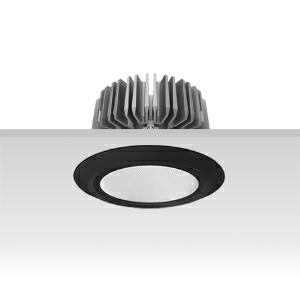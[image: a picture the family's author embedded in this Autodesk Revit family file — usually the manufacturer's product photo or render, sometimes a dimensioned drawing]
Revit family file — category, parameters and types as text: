
# Revit family: 3f_filippi_-_3f_reno_bianco_ampio_3f_filippi_-_30345_a01047_-_3f_reno_150_wh_2000-930_wide___smp_bk_7763
name_source: partatom
category: Lighting Fixtures
units: mm (PartAtom-declared; Revit-internal decimal feet)

## family parameters
Cut with Voids When Loaded = No
Host = Face
Light Source = No
Part Type = Normal
Room Calculation Point = No
Round Connector Dimension = Use Diameter
Shared = No

## types (1)
- 3F Filippi - 3F Reno Bianco Ampio (1 x LED, 1652 lm, 24 W, 3000 K)
    Apparent Load = 24 VA
    Approval mark = CE
    CIE Flux Codes = 73 92 98 100 100
    Color Rendering = 90
    Color Temperature = 3000 K
    Control Gear = Electronic ballast
    Default Elevation = 1800 mm
    Description = ILLUMINOTECHNICAL
Luminous efficiency 100% (DLOR 100%, ULOR 0%).
Initial luminous flux of the luminaire 1652 lm.
Direct symmetric wide distribution.
Installation Interdistance Transv.D = 1.01 x hu - Long.D = 1.00 x hu.
Tabular UGR (CIE 117 - 4H-8H; S=0.25H; 70/50/20): RUG 23.3 - 23.3.
Beam angle: 70° - 70°.
Luminous efficacy 69 lm/W.
Lifetime (L90/B10): 30000 h. (tq+25°C)
Lifetime (L85/B10): 50000 h. (tq+25°C)
Lifetime (L70/B10): 80000 h. (tq+25°C)
Sudden decreased luminous flux after 50000 hours: 0% (C0).
Photobiological safety in compliance with IEC/TR 62778: RG0 risk exempt, (IEC 62471).
In compliance with IEC/EN 62722-2-1 - IEC/EN 62717 standards.

SOURCE
Compact LED module 2000/930.
Energy efficiency class (UE 2019/2020 - UE 2019/2015): E.
CIE 13.3 Colour rendering index: CRI >90 (R9 >50%).
IES TM-30 Fidelity Index: Rf = 92 Rg = 101.
CCT nominal colour temperature 3000 K.
Colour initial tolerance (MacAdam): SDCM 3.
Zhaga Book 3 compliant.

MECHANICAL
Passive heat dissipator in die-casting aluminium, oversized, for optimum thermal management of the LED module.
Parabolic element with graduated/concentric rings in white polycarbonate.
Transparent external lens with glossy and satin differentiated surfaces, with a cooling and anti-insect system in methacrylate (PMMA).
Fastening spring clips in stainless steel.
Dimensions: diameter 176 mm, height 111 mm. Weight 0.75 kg.
IP44 protection degree for exposed part, IP20 for recessed part.
Mechanical strength to impacts IK05 (0.7 joule).
Glow-wire test resistance 650°C.

ELECTRICAL
Wiring on a separate unit.
Halogen Free electronic wiring 230V-50/60Hz, power factor 0.95, THD <25%, constant output current, SELV, class II, 1 driver.
Power of the luminaire 24 W.
ENEC - CE.
SAFE FLICKER: PstLM=<1 and SVM=<0.4 (IEC TR 61547-1 and IEC TR 63158), to ensure a more comfortable and safe light.
Luminaire compliant with EN 60598-2-22 for power supply from a centralised emergency system CPSS (Central Power Supply System), not incorporated in the luminaire - high risk areas excluded. The default power and flux are 100% in AC and 100% in DC.
Ambient temperature from 0°C to +25°C.
Temperature class T6 max 85°C.
Relative humidity UR: <85%.

INSTALLATION
Pull-up recessed fitting.
False ceiling carving: 150 mm.
All accessories dedicated to this product are available on the Catalog and on our website www.3F-Filippi.com.

ACCESSORIES
A01047 - Anti-glare microprismatic SMP diffuser in methacrylate (PMMA), locked and in line with the trim, in black polycarbonate.

APPLICATIONS
Suitable product for food production plants (HACCP), IFS (Food Version 6), BRC (GSFS Food Version 7).
Environments: architectural, commercial, exhibition areas, transit areas, corridors, shops, display windows, service areas.
In false ceilings with narrow voids.

WARNING
Luminaire designed for disposal/recycling at end-of-life.
Replaceable (LED only) light source by a professional. Replaceable control gear by a professional.
    Height = 0 mm  [stored 0 ft]
    Lamp = 1 x LED
    Lamp Light Flux = 1652 lm
    Lamp Power = 24 W
    Lamp count = 1
    Length = 176 mm
    Lifetime = 50000 h
    Luminous efficacy = 69 lm/W
    Manufacturer = 3F Filippi
    ModVariant = No
    Model = 3F Filippi - 30345+A01047 - 3F Reno 150 WH 2000-930 WIDE + SMP BK
    Mounting Place = Ceiling
    Mounting Type = Recessed
    Number of Poles = 1
    OnlyDefault = Yes
    Power Factor = 1
    Product Name = 3F Filippi - 3F Reno Bianco Ampio
    Product group = recessed luminaire
    ProductGroupID = 4
    Protection Class = Protection class II
    Protection Degree = IP 20
    RLX_Detail_Level = 1
    RLX_Emergency_Light_Flux = 0 lm
    RLX_Emergency_Type = 0
    RLX_Emergency_Type_DB = No
    RlxData = <blob elided: 87077 chars, md5=64cae987>
    Socket = socket
    Standby Power = 0 W
    System Light Flux = 1652 lm
    System Power = 24 W
    Type Comments = Product without accessories
    Type Image = 3ffilippi_3f_reno_150_bk_vs_smp.jpg
    URL = http://relux.com
    VarID = ---
    Voltage = 0 V
    Weight = 0.00 kg
    Width = 0 mm  [stored 0 ft]

note: [stored X ft] marks values corroborated as IEEE doubles in the binary element streams (Revit-internal decimal feet)

## geometry (parser evidence)
native form markers: Blend x4, Sweep x10
no freeform markers — native parametric forms only
